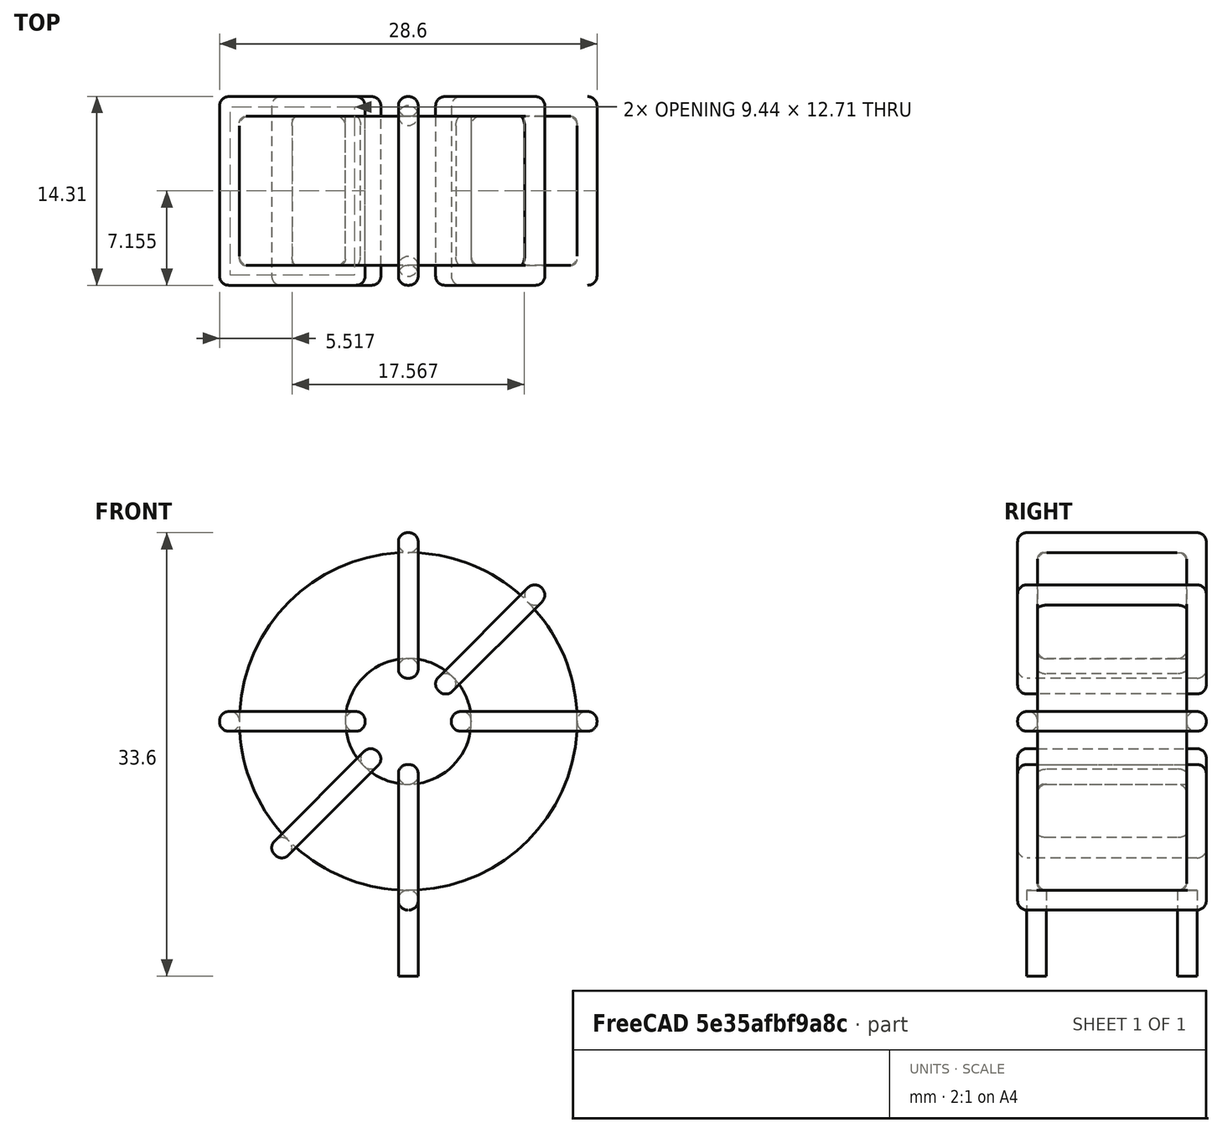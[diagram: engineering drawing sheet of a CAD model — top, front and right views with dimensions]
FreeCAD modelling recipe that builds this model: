
FCSTD DOCUMENT  (FreeCAD 0.16R6703 (Git))
Label: L_Toroid_Vertical_L28.6mm_W14.3mm_P11.43mm_Bourns_5700series
License: All rights reserved
LicenseURL: http://en.wikipedia.org/wiki/All_rights_reserved
objects: Sketcher::SketchObject×6, PartDesign::Pad×6, PartDesign::Fillet×5, Spreadsheet::Sheet×1
note: 23 computed .brp shape members not serialized (recipe doc carries the construction recipe); baked Part::Feature solids carry a one-line shape summary decoded from their .brp

FEATURE [Spreadsheet::Sheet] Spreadsheet  label="dimensions"
  cells = A1=Wx; B1(Wx)=28.6; C1(WW)=9.533333333333333; D1=28.6; A2=Wy; B2(Wy)=14.3; D2=14.3; A3=RM; B3(RMx)=11.43; C3(RMy)=0; A4=d_wire; B4(d_wire)=1.5; A5=H; B5(H)=28.6; A6=offsetx; B6(offsetx)=14.3
FEATURE [Sketcher::SketchObject] Sketch
  Placement = pos=(0,-5.715,0) rot=(1,0,0;1.5708rad)
  expr: Placement.Base.y = -Spreadsheet.RMx / 2
  expr: Constraints[0] = Spreadsheet.Wx / 2 - Spreadsheet.d_wire
  expr: Constraints[4] = Spreadsheet.WW / 2
  expr: Constraints[2] = Spreadsheet.Wx / 2 + Spreadsheet.d_wire + 0.5
  sketch-geometry (2):
    g0: Circle CenterX=0 CenterY=16.3 CenterZ=0 NormalX=0 NormalY=0 NormalZ=1 Radius=12.8
    g1: Circle CenterX=0 CenterY=16.3 CenterZ=0 NormalX=0 NormalY=0 NormalZ=1 Radius=4.76667
  constraints (5):
    c: Radius(g0) = 12.8
    c: DistanceX(g-1,g0) = 0
    c: DistanceY(g-1,g0) = 16.3
    c: Coincident(g1,g0)
    c: Radius(g1) = 4.76667
FEATURE [PartDesign::Pad] Pad
  Length = 11.3
  Length2 = 100
  Midplane = true
  Placement = pos=(0,-5.715,0) rot=(1,0,0;1.5708rad)
  Sketch = -> Sketch
  Type = 0
  expr: Length = Spreadsheet.Wy - 2 * Spreadsheet.d_wire
FEATURE [Sketcher::SketchObject] Sketch001
  Placement = pos=(0,0,2) rot=(0,0,1;0rad)
  expr: Placement.Base.z = 0.5 + Spreadsheet.d_wire
  expr: Constraints[4] = Spreadsheet.RMy
  expr: Constraints[2] = -Spreadsheet.RMx
  expr: Constraints[1] = Spreadsheet.d_wire / 2
  sketch-geometry (2):
    g0: Circle CenterX=0 CenterY=0 CenterZ=0 NormalX=0 NormalY=0 NormalZ=1 Radius=0.75
    g1: Circle CenterX=0 CenterY=-11.43 CenterZ=0 NormalX=0 NormalY=0 NormalZ=1 Radius=0.75
  constraints (5):
    c: Equal(g0,g1)
    c: Radius(g0) = 0.75
    c: DistanceY(g-1,g1) = -11.43
    c: Coincident(g0,g-1)
    c: DistanceX(g-1,g1) = 0
FEATURE [PartDesign::Pad] Pad001
  Length = 1.5
  Length2 = 5
  Placement = pos=(0,0,2) rot=(0,0,1;0rad)
  Reversed = true
  Sketch = -> Sketch001
  Type = 4
  expr: Length2 = 3.5 + Spreadsheet.d_wire
  expr: Length = Spreadsheet.d_wire
FEATURE [PartDesign::Fillet] Fillet
  Base = -> Pad [Edge6,Edge3,Edge2]
  Placement = pos=(0,-5.715,0) rot=(1,0,0;1.5708rad)
  Radius = 0.5
FEATURE [Sketcher::SketchObject] Sketch003
  Placement = pos=(0,1.435,16.3) rot=(1,0,0;3.14159rad)
  expr: Constraints[18] = Spreadsheet.d_wire
  expr: Constraints[16] = Spreadsheet.d_wire
  expr: Constraints[19] = Spreadsheet.d_wire
  expr: Constraints[17] = Spreadsheet.d_wire
  expr: Placement.Base.y = -1 * (Spreadsheet.RMx - Spreadsheet.Wy) / 2
  expr: Constraints[21] = (Spreadsheet.Wx - Spreadsheet.WW) / 2 - Spreadsheet.d_wire
  expr: Constraints[22] = Spreadsheet.Wx / 2 - Spreadsheet.d_wire
  expr: Constraints[43] = Spreadsheet.d_wire
  expr: Constraints[48] = Spreadsheet.Wx - Spreadsheet.d_wire * 2
  expr: Constraints[49] = Spreadsheet.Wy
  expr: Placement.Base.z = Spreadsheet.Wx / 2 + Spreadsheet.d_wire + 0.5
  sketch-geometry (16):
    g0: LineSegment StartX=-3.26667 StartY=0 StartZ=0 EndX=-14.3 EndY=0 EndZ=0
    g1: LineSegment StartX=-14.3 StartY=0 StartZ=0 EndX=-14.3 EndY=14.3 EndZ=0
    g2: LineSegment StartX=-14.3 StartY=14.3 StartZ=0 EndX=-3.26667 EndY=14.3 EndZ=0
    g3: LineSegment StartX=-3.26667 StartY=14.3 StartZ=0 EndX=-3.26667 EndY=0 EndZ=0
    g4: LineSegment StartX=-12.8 StartY=12.8 StartZ=0 EndX=-4.76667 EndY=12.8 EndZ=0
    g5: LineSegment StartX=-4.76667 StartY=12.8 StartZ=0 EndX=-4.76667 EndY=1.5 EndZ=0
    g6: LineSegment StartX=-4.76667 StartY=1.5 StartZ=0 EndX=-12.8 EndY=1.5 EndZ=0
    g7: LineSegment StartX=-12.8 StartY=1.5 StartZ=0 EndX=-12.8 EndY=12.8 EndZ=0
    g8: LineSegment StartX=3.26667 StartY=14.3 StartZ=0 EndX=14.3 EndY=14.3 EndZ=0
    g9: LineSegment StartX=14.3 StartY=14.3 StartZ=0 EndX=14.3 EndY=0 EndZ=0
    g10: LineSegment StartX=14.3 StartY=0 StartZ=0 EndX=3.26667 EndY=0 EndZ=0
    g11: LineSegment StartX=3.26667 StartY=0 StartZ=0 EndX=3.26667 EndY=14.3 EndZ=0
    g12: LineSegment StartX=4.76667 StartY=12.8 StartZ=0 EndX=12.8 EndY=12.8 EndZ=0
    g13: LineSegment StartX=12.8 StartY=12.8 StartZ=0 EndX=12.8 EndY=1.5 EndZ=0
    g14: LineSegment StartX=12.8 StartY=1.5 StartZ=0 EndX=4.76667 EndY=1.5 EndZ=0
    g15: LineSegment StartX=4.76667 StartY=1.5 StartZ=0 EndX=4.76667 EndY=12.8 EndZ=0
  constraints (50):
    c: Horizontal(g0)
    c: Coincident(g1,g0)
    c: Vertical(g1)
    c: Coincident(g2,g1)
    c: Horizontal(g2)
    c: Coincident(g3,g2)
    c: Coincident(g3,g0)
    c: Vertical(g3)
    c: Coincident(g4,g5)
    c: Coincident(g5,g6)
    c: Coincident(g6,g7)
    c: Coincident(g7,g4)
    c: Horizontal(g4)
    c: Horizontal(g6)
    c: Vertical(g5)
    c: Vertical(g7)
    c: DistanceX(g1,g4) = 1.5
    c: DistanceY(g4,g1) = 1.5
    c: DistanceX(g5,g0) = 1.5
    c: DistanceY(g0,g5) = 1.5
    c: DistanceY(g-1,g0) = 0
    c: DistanceX(g6,g6) = 8.03333
    c: DistanceX(g6,g-1) = 12.8
    c: Coincident(g8,g9)
    c: Coincident(g9,g10)
    c: Coincident(g10,g11)
    c: Coincident(g11,g8)
    c: Horizontal(g8)
    c: Horizontal(g10)
    c: Vertical(g9)
    c: Vertical(g11)
    c: Coincident(g12,g13)
    c: Coincident(g13,g14)
    c: Coincident(g14,g15)
    c: Coincident(g15,g12)
    c: Horizontal(g12)
    c: Horizontal(g14)
    c: Vertical(g13)
    c: Vertical(g15)
    c: DistanceY(g8,g2) = 0
    c: DistanceY(g10,g0) = 0
    c: DistanceY(g14,g5) = 0
    c: DistanceY(g12,g4) = 0
    c: DistanceX(g8,g12) = 1.5
    c: Equal(g8,g2)
    c: Equal(g12,g4)
    c: Equal(g9,g1)
    c: Equal(g13,g7)
    c: DistanceX(g4,g12) = 25.6
    c: DistanceY(g0,g1) = 14.3
FEATURE [PartDesign::Pad] Pad002
  Length = 1.5
  Length2 = 100
  Midplane = true
  Placement = pos=(0,1.435,16.3) rot=(1,0,0;3.14159rad)
  Sketch = -> Sketch003
  Type = 0
  expr: Length = Spreadsheet.d_wire
FEATURE [PartDesign::Fillet] Fillet001
  Base = -> Pad002 [Edge38,Edge41,Edge42,Edge43,Edge29,Edge32,Edge33,Edge34,Edge25,Edge35,Edge36,Edge13,Edge14,Edge15,Edge16,Edge17,Edge18,Edge19,Edge1,Edge2,Edge3,Edge4,Edge5,Edge6,Edge7,Edge37,Edge39,Edge40,Edge20,Edge23,Edge24,Edge21,Edge22,Edge8,Edge9,Edge10,Edge11,Edge12,Edge26,Edge27,+8 more]
  Placement = pos=(0,1.435,16.3) rot=(1,0,0;3.14159rad)
  Radius = 0.705
  expr: Radius = Spreadsheet.d_wire * 0.47
FEATURE [Sketcher::SketchObject] Sketch004
  Placement = pos=(0,1.435,16.3) rot=(0.92388,0,0.382683;3.14159rad)
  expr: Constraints[18] = Spreadsheet.d_wire
  expr: Constraints[16] = Spreadsheet.d_wire
  expr: Constraints[19] = Spreadsheet.d_wire
  expr: Constraints[17] = Spreadsheet.d_wire
  expr: Placement.Base.y = -1 * (Spreadsheet.RMx - Spreadsheet.Wy) / 2
  expr: Constraints[21] = (Spreadsheet.Wx - Spreadsheet.WW) / 2 - Spreadsheet.d_wire
  expr: Constraints[22] = Spreadsheet.Wx / 2 - Spreadsheet.d_wire
  expr: Constraints[43] = Spreadsheet.d_wire
  expr: Constraints[48] = Spreadsheet.Wx - 2 * Spreadsheet.d_wire
  expr: Constraints[49] = Spreadsheet.Wy
  expr: Placement.Base.z = Spreadsheet.Wx / 2 + Spreadsheet.d_wire + 0.5
  sketch-geometry (16):
    g0: LineSegment StartX=-3.26667 StartY=0 StartZ=0 EndX=-14.3 EndY=0 EndZ=0
    g1: LineSegment StartX=-14.3 StartY=0 StartZ=0 EndX=-14.3 EndY=14.3 EndZ=0
    g2: LineSegment StartX=-14.3 StartY=14.3 StartZ=0 EndX=-3.26667 EndY=14.3 EndZ=0
    g3: LineSegment StartX=-3.26667 StartY=14.3 StartZ=0 EndX=-3.26667 EndY=0 EndZ=0
    g4: LineSegment StartX=-12.8 StartY=12.8 StartZ=0 EndX=-4.76667 EndY=12.8 EndZ=0
    g5: LineSegment StartX=-4.76667 StartY=12.8 StartZ=0 EndX=-4.76667 EndY=1.5 EndZ=0
    g6: LineSegment StartX=-4.76667 StartY=1.5 StartZ=0 EndX=-12.8 EndY=1.5 EndZ=0
    g7: LineSegment StartX=-12.8 StartY=1.5 StartZ=0 EndX=-12.8 EndY=12.8 EndZ=0
    g8: LineSegment StartX=3.26667 StartY=14.3 StartZ=0 EndX=14.3 EndY=14.3 EndZ=0
    g9: LineSegment StartX=14.3 StartY=14.3 StartZ=0 EndX=14.3 EndY=0 EndZ=0
    g10: LineSegment StartX=14.3 StartY=0 StartZ=0 EndX=3.26667 EndY=0 EndZ=0
    g11: LineSegment StartX=3.26667 StartY=0 StartZ=0 EndX=3.26667 EndY=14.3 EndZ=0
    g12: LineSegment StartX=4.76667 StartY=12.8 StartZ=0 EndX=12.8 EndY=12.8 EndZ=0
    g13: LineSegment StartX=12.8 StartY=12.8 StartZ=0 EndX=12.8 EndY=1.5 EndZ=0
    g14: LineSegment StartX=12.8 StartY=1.5 StartZ=0 EndX=4.76667 EndY=1.5 EndZ=0
    g15: LineSegment StartX=4.76667 StartY=1.5 StartZ=0 EndX=4.76667 EndY=12.8 EndZ=0
  constraints (50):
    c: Horizontal(g0)
    c: Coincident(g1,g0)
    c: Vertical(g1)
    c: Coincident(g2,g1)
    c: Horizontal(g2)
    c: Coincident(g3,g2)
    c: Coincident(g3,g0)
    c: Vertical(g3)
    c: Coincident(g4,g5)
    c: Coincident(g5,g6)
    c: Coincident(g6,g7)
    c: Coincident(g7,g4)
    c: Horizontal(g4)
    c: Horizontal(g6)
    c: Vertical(g5)
    c: Vertical(g7)
    c: DistanceX(g1,g4) = 1.5
    c: DistanceY(g4,g1) = 1.5
    c: DistanceX(g5,g0) = 1.5
    c: DistanceY(g0,g5) = 1.5
    c: DistanceY(g-1,g0) = 0
    c: DistanceX(g6,g6) = 8.03333
    c: DistanceX(g6,g-1) = 12.8
    c: Coincident(g8,g9)
    c: Coincident(g9,g10)
    c: Coincident(g10,g11)
    c: Coincident(g11,g8)
    c: Horizontal(g8)
    c: Horizontal(g10)
    c: Vertical(g9)
    c: Vertical(g11)
    c: Coincident(g12,g13)
    c: Coincident(g13,g14)
    c: Coincident(g14,g15)
    c: Coincident(g15,g12)
    c: Horizontal(g12)
    c: Horizontal(g14)
    c: Vertical(g13)
    c: Vertical(g15)
    c: DistanceY(g8,g2) = 0
    c: DistanceY(g10,g0) = 0
    c: DistanceY(g14,g5) = 0
    c: DistanceY(g12,g4) = 0
    c: DistanceX(g8,g12) = 1.5
    c: Equal(g8,g2)
    c: Equal(g12,g4)
    c: Equal(g9,g1)
    c: Equal(g13,g7)
    c: DistanceX(g4,g12) = 25.6
    c: DistanceY(g0,g1) = 14.3
FEATURE [PartDesign::Pad] Pad003
  Length = 1.5
  Length2 = 100
  Midplane = true
  Placement = pos=(0,1.435,16.3) rot=(0.92388,0,0.382683;3.14159rad)
  Sketch = -> Sketch004
  Type = 0
  expr: Length = Spreadsheet.d_wire
FEATURE [PartDesign::Fillet] Fillet002
  Base = -> Pad003 [Edge38,Edge41,Edge42,Edge43,Edge29,Edge32,Edge33,Edge34,Edge25,Edge35,Edge36,Edge13,Edge14,Edge15,Edge16,Edge17,Edge18,Edge19,Edge1,Edge2,Edge3,Edge4,Edge5,Edge6,Edge7,Edge37,Edge39,Edge40,Edge20,Edge23,Edge24,Edge21,Edge22,Edge8,Edge9,Edge10,Edge11,Edge12,Edge26,Edge27,+8 more]
  Placement = pos=(0,1.435,16.3) rot=(0.92388,0,0.382683;3.14159rad)
  Radius = 0.705
  expr: Radius = Spreadsheet.d_wire * 0.47
FEATURE [Sketcher::SketchObject] Sketch005
  Placement = pos=(0,1.435,16.3) rot=(0.92388,0,-0.382683;3.14159rad)
  expr: Constraints[18] = Spreadsheet.d_wire
  expr: Constraints[16] = Spreadsheet.d_wire
  expr: Constraints[19] = Spreadsheet.d_wire
  expr: Constraints[17] = Spreadsheet.d_wire
  expr: Placement.Base.y = -1 * (Spreadsheet.RMx - Spreadsheet.Wy) / 2
  expr: Constraints[21] = (Spreadsheet.Wx - Spreadsheet.WW) / 2 - Spreadsheet.d_wire
  expr: Constraints[22] = Spreadsheet.Wx / 2 - Spreadsheet.d_wire
  expr: Constraints[43] = Spreadsheet.d_wire
  expr: Constraints[48] = Spreadsheet.Wx - 2 * Spreadsheet.d_wire
  expr: Constraints[49] = Spreadsheet.Wy
  expr: Placement.Base.z = Spreadsheet.Wx / 2 + Spreadsheet.d_wire + 0.5
  sketch-geometry (16):
    g0: LineSegment StartX=-3.26667 StartY=0 StartZ=0 EndX=-14.3 EndY=0 EndZ=0
    g1: LineSegment StartX=-14.3 StartY=0 StartZ=0 EndX=-14.3 EndY=14.3 EndZ=0
    g2: LineSegment StartX=-14.3 StartY=14.3 StartZ=0 EndX=-3.26667 EndY=14.3 EndZ=0
    g3: LineSegment StartX=-3.26667 StartY=14.3 StartZ=0 EndX=-3.26667 EndY=0 EndZ=0
    g4: LineSegment StartX=-12.8 StartY=12.8 StartZ=0 EndX=-4.76667 EndY=12.8 EndZ=0
    g5: LineSegment StartX=-4.76667 StartY=12.8 StartZ=0 EndX=-4.76667 EndY=1.5 EndZ=0
    g6: LineSegment StartX=-4.76667 StartY=1.5 StartZ=0 EndX=-12.8 EndY=1.5 EndZ=0
    g7: LineSegment StartX=-12.8 StartY=1.5 StartZ=0 EndX=-12.8 EndY=12.8 EndZ=0
    g8: LineSegment StartX=3.26667 StartY=14.3 StartZ=0 EndX=14.3 EndY=14.3 EndZ=0
    g9: LineSegment StartX=14.3 StartY=14.3 StartZ=0 EndX=14.3 EndY=0 EndZ=0
    g10: LineSegment StartX=14.3 StartY=0 StartZ=0 EndX=3.26667 EndY=0 EndZ=0
    g11: LineSegment StartX=3.26667 StartY=0 StartZ=0 EndX=3.26667 EndY=14.3 EndZ=0
    g12: LineSegment StartX=4.76667 StartY=12.8 StartZ=0 EndX=12.8 EndY=12.8 EndZ=0
    g13: LineSegment StartX=12.8 StartY=12.8 StartZ=0 EndX=12.8 EndY=1.5 EndZ=0
    g14: LineSegment StartX=12.8 StartY=1.5 StartZ=0 EndX=4.76667 EndY=1.5 EndZ=0
    g15: LineSegment StartX=4.76667 StartY=1.5 StartZ=0 EndX=4.76667 EndY=12.8 EndZ=0
  constraints (50):
    c: Horizontal(g0)
    c: Coincident(g1,g0)
    c: Vertical(g1)
    c: Coincident(g2,g1)
    c: Horizontal(g2)
    c: Coincident(g3,g2)
    c: Coincident(g3,g0)
    c: Vertical(g3)
    c: Coincident(g4,g5)
    c: Coincident(g5,g6)
    c: Coincident(g6,g7)
    c: Coincident(g7,g4)
    c: Horizontal(g4)
    c: Horizontal(g6)
    c: Vertical(g5)
    c: Vertical(g7)
    c: DistanceX(g1,g4) = 1.5
    c: DistanceY(g4,g1) = 1.5
    c: DistanceX(g5,g0) = 1.5
    c: DistanceY(g0,g5) = 1.5
    c: DistanceY(g-1,g0) = 0
    c: DistanceX(g6,g6) = 8.03333
    c: DistanceX(g6,g-1) = 12.8
    c: Coincident(g8,g9)
    c: Coincident(g9,g10)
    c: Coincident(g10,g11)
    c: Coincident(g11,g8)
    c: Horizontal(g8)
    c: Horizontal(g10)
    c: Vertical(g9)
    c: Vertical(g11)
    c: Coincident(g12,g13)
    c: Coincident(g13,g14)
    c: Coincident(g14,g15)
    c: Coincident(g15,g12)
    c: Horizontal(g12)
    c: Horizontal(g14)
    c: Vertical(g13)
    c: Vertical(g15)
    c: DistanceY(g8,g2) = 0
    c: DistanceY(g10,g0) = 0
    c: DistanceY(g14,g5) = 0
    c: DistanceY(g12,g4) = 0
    c: DistanceX(g8,g12) = 1.5
    c: Equal(g8,g2)
    c: Equal(g12,g4)
    c: Equal(g9,g1)
    c: Equal(g13,g7)
    c: DistanceX(g4,g12) = 25.6
    c: DistanceY(g0,g1) = 14.3
FEATURE [PartDesign::Pad] Pad004
  Length = 1.5
  Length2 = 100
  Midplane = true
  Placement = pos=(0,1.435,16.3) rot=(0.92388,0,-0.382683;3.14159rad)
  Sketch = -> Sketch005
  Type = 0
  expr: Length = Spreadsheet.d_wire
FEATURE [PartDesign::Fillet] Fillet003
  Base = -> Pad004 [Edge38,Edge41,Edge42,Edge43,Edge29,Edge32,Edge33,Edge34,Edge25,Edge35,Edge36,Edge13,Edge14,Edge15,Edge16,Edge17,Edge18,Edge19,Edge1,Edge2,Edge3,Edge4,Edge5,Edge6,Edge7,Edge37,Edge39,Edge40,Edge20,Edge23,Edge24,Edge21,Edge22,Edge8,Edge9,Edge10,Edge11,Edge12,Edge26,Edge27,+8 more]
  Placement = pos=(0,1.435,16.3) rot=(0.92388,0,-0.382683;3.14159rad)
  Radius = 0.705
  expr: Radius = Spreadsheet.d_wire * 0.47
FEATURE [Sketcher::SketchObject] Sketch006
  Placement = pos=(0,1.435,16.3) rot=(0.707107,0,0.707107;3.14159rad)
  expr: Constraints[18] = Spreadsheet.d_wire
  expr: Constraints[16] = Spreadsheet.d_wire
  expr: Constraints[19] = Spreadsheet.d_wire
  expr: Constraints[17] = Spreadsheet.d_wire
  expr: Placement.Base.y = -1 * (Spreadsheet.RMx - Spreadsheet.Wy) / 2
  expr: Constraints[21] = (Spreadsheet.Wx - Spreadsheet.WW) / 2 - Spreadsheet.d_wire
  expr: Constraints[22] = Spreadsheet.Wx / 2 - Spreadsheet.d_wire
  expr: Constraints[43] = Spreadsheet.d_wire
  expr: Constraints[48] = Spreadsheet.Wx - Spreadsheet.d_wire * 2
  expr: Constraints[49] = Spreadsheet.Wy
  expr: Placement.Base.z = Spreadsheet.Wx / 2 + Spreadsheet.d_wire + 0.5
  sketch-geometry (16):
    g0: LineSegment StartX=-3.26667 StartY=0 StartZ=0 EndX=-14.3 EndY=0 EndZ=0
    g1: LineSegment StartX=-14.3 StartY=0 StartZ=0 EndX=-14.3 EndY=14.3 EndZ=0
    g2: LineSegment StartX=-14.3 StartY=14.3 StartZ=0 EndX=-3.26667 EndY=14.3 EndZ=0
    g3: LineSegment StartX=-3.26667 StartY=14.3 StartZ=0 EndX=-3.26667 EndY=0 EndZ=0
    g4: LineSegment StartX=-12.8 StartY=12.8 StartZ=0 EndX=-4.76667 EndY=12.8 EndZ=0
    g5: LineSegment StartX=-4.76667 StartY=12.8 StartZ=0 EndX=-4.76667 EndY=1.5 EndZ=0
    g6: LineSegment StartX=-4.76667 StartY=1.5 StartZ=0 EndX=-12.8 EndY=1.5 EndZ=0
    g7: LineSegment StartX=-12.8 StartY=1.5 StartZ=0 EndX=-12.8 EndY=12.8 EndZ=0
    g8: LineSegment StartX=3.26667 StartY=14.3 StartZ=0 EndX=14.3 EndY=14.3 EndZ=0
    g9: LineSegment StartX=14.3 StartY=14.3 StartZ=0 EndX=14.3 EndY=0 EndZ=0
    g10: LineSegment StartX=14.3 StartY=0 StartZ=0 EndX=3.26667 EndY=0 EndZ=0
    g11: LineSegment StartX=3.26667 StartY=0 StartZ=0 EndX=3.26667 EndY=14.3 EndZ=0
    g12: LineSegment StartX=4.76667 StartY=12.8 StartZ=0 EndX=12.8 EndY=12.8 EndZ=0
    g13: LineSegment StartX=12.8 StartY=12.8 StartZ=0 EndX=12.8 EndY=1.5 EndZ=0
    g14: LineSegment StartX=12.8 StartY=1.5 StartZ=0 EndX=4.76667 EndY=1.5 EndZ=0
    g15: LineSegment StartX=4.76667 StartY=1.5 StartZ=0 EndX=4.76667 EndY=12.8 EndZ=0
  constraints (50):
    c: Horizontal(g0)
    c: Coincident(g1,g0)
    c: Vertical(g1)
    c: Coincident(g2,g1)
    c: Horizontal(g2)
    c: Coincident(g3,g2)
    c: Coincident(g3,g0)
    c: Vertical(g3)
    c: Coincident(g4,g5)
    c: Coincident(g5,g6)
    c: Coincident(g6,g7)
    c: Coincident(g7,g4)
    c: Horizontal(g4)
    c: Horizontal(g6)
    c: Vertical(g5)
    c: Vertical(g7)
    c: DistanceX(g1,g4) = 1.5
    c: DistanceY(g4,g1) = 1.5
    c: DistanceX(g5,g0) = 1.5
    c: DistanceY(g0,g5) = 1.5
    c: DistanceY(g-1,g0) = 0
    c: DistanceX(g6,g6) = 8.03333
    c: DistanceX(g6,g-1) = 12.8
    c: Coincident(g8,g9)
    c: Coincident(g9,g10)
    c: Coincident(g10,g11)
    c: Coincident(g11,g8)
    c: Horizontal(g8)
    c: Horizontal(g10)
    c: Vertical(g9)
    c: Vertical(g11)
    c: Coincident(g12,g13)
    c: Coincident(g13,g14)
    c: Coincident(g14,g15)
    c: Coincident(g15,g12)
    c: Horizontal(g12)
    c: Horizontal(g14)
    c: Vertical(g13)
    c: Vertical(g15)
    c: DistanceY(g8,g2) = 0
    c: DistanceY(g10,g0) = 0
    c: DistanceY(g14,g5) = 0
    c: DistanceY(g12,g4) = 0
    c: DistanceX(g8,g12) = 1.5
    c: Equal(g8,g2)
    c: Equal(g12,g4)
    c: Equal(g9,g1)
    c: Equal(g13,g7)
    c: DistanceX(g4,g12) = 25.6
    c: DistanceY(g0,g1) = 14.3
FEATURE [PartDesign::Pad] Pad005
  Length = 1.5
  Length2 = 100
  Midplane = true
  Placement = pos=(0,1.435,16.3) rot=(0.707107,0,0.707107;3.14159rad)
  Sketch = -> Sketch006
  Type = 0
  expr: Length = Spreadsheet.d_wire
FEATURE [PartDesign::Fillet] Fillet004
  Base = -> Pad005 [Edge38,Edge41,Edge42,Edge43,Edge29,Edge32,Edge33,Edge34,Edge25,Edge35,Edge36,Edge13,Edge14,Edge15,Edge16,Edge17,Edge18,Edge19,Edge1,Edge2,Edge3,Edge4,Edge5,Edge6,Edge7,Edge37,Edge39,Edge40,Edge20,Edge23,Edge24,Edge21,Edge22,Edge8,Edge9,Edge10,Edge11,Edge12,Edge26,Edge27,+8 more]
  Placement = pos=(0,1.435,16.3) rot=(0.707107,0,0.707107;3.14159rad)
  Radius = 0.705
  expr: Radius = Spreadsheet.d_wire * 0.47
